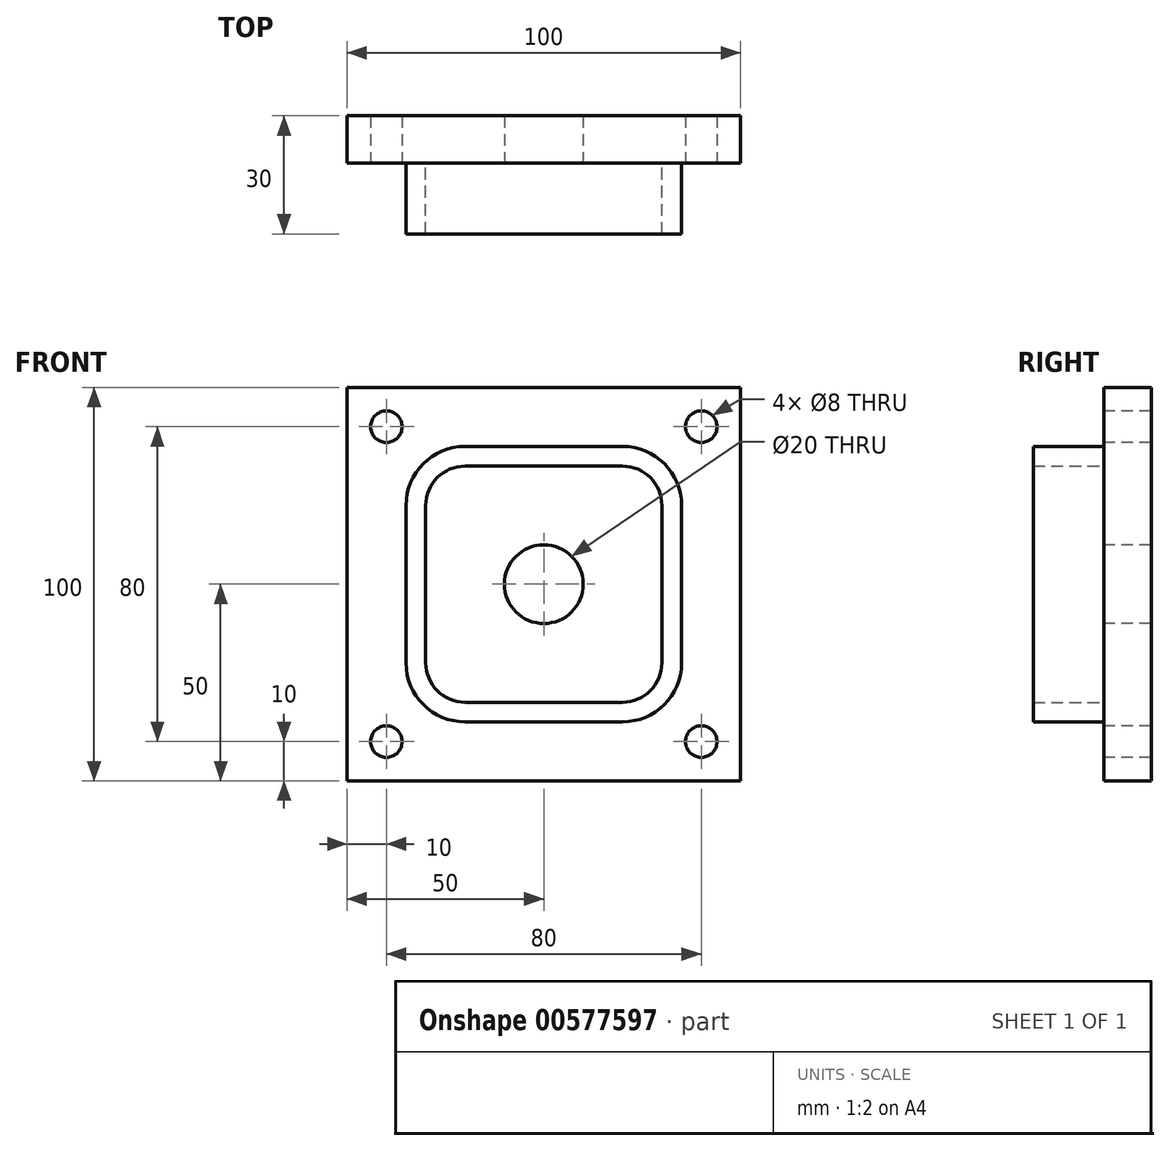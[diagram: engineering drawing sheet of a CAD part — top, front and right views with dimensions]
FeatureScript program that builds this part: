
annotation { "Feature Type Name" : "Feature", "Feature Type Description" : "" }
export const myFeature = defineFeature(function(context is Context, id is Id, definition is map)
    precondition{}
    {
        {
            var Q0;
            Q0=qCreatedBy(makeId("Front.planeOp"),FACE);
            var sketch = newSketch(context, id + "F0", { "sketchPlane" : qUnion([Q0])});
            skLineSegment(sketch, "E0.bottom", {"start": v(0, 0) * mm, "end": v(-100, 0) * mm});
            skLineSegment(sketch, "E0.top", {"start": v(0, 100) * mm, "end": v(-100, 100) * mm});
            skLineSegment(sketch, "E0.left", {"start": v(0, 0) * mm, "end": v(0, 100) * mm});
            skLineSegment(sketch, "E0.right", {"start": v(-100, 0) * mm, "end": v(-100, 100) * mm});
            skSolve(sketch);
        }
        {
            var Q0;
            Q0=makeQuery(id+"F0.imprint","IMPRINT",FACE,{"disambiguationData":[TD([[makeQuery(id+"F0.imprint","IMPRINT",EDGE,{"derivedFrom":sQuery(id+"F0.wireOp",EDGE,"E0.bottom")}),-1.0]])]});
            extrude(context, id + "F1", {"entities" : qUnion([Q0]), "depth" : 12 * mm, "offsetDistance" : 25 * mm});
        }
        {
            var Q0;
            Q0=makeQuery(id+"F1.opExtrude","CAP_FACE",FACE,{"disambiguationData":[OSD([sQuery(id+"F0.wireOp",EDGE,"E0.bottom"),sQuery(id+"F0.wireOp",EDGE,"E0.top"),sQuery(id+"F0.wireOp",EDGE,"E0.left"),sQuery(id+"F0.wireOp",EDGE,"E0.right")])],"isStart":false});
            var sketch = newSketch(context, id + "F2", { "sketchPlane" : qUnion([Q0])});
            skLineSegment(sketch, "E1.bottom", {"start": v(-90, 90) * mm, "end": v(-10, 90) * mm, "construction": true});
            skLineSegment(sketch, "E1.top", {"start": v(-90, 10) * mm, "end": v(-10, 10) * mm, "construction": true});
            skLineSegment(sketch, "E1.left", {"start": v(-90, 90) * mm, "end": v(-90, 10) * mm, "construction": true});
            skLineSegment(sketch, "E1.right", {"start": v(-10, 90) * mm, "end": v(-10, 10) * mm, "construction": true});
            skCircle(sketch, "E2", {"center": v(-90, 90) * mm, "radius": 4 * mm});
            skCircle(sketch, "E3", {"center": v(-90, 10) * mm, "radius": 4 * mm});
            skCircle(sketch, "E4", {"center": v(-10, 90) * mm, "radius": 4 * mm});
            skCircle(sketch, "E5", {"center": v(-10, 10) * mm, "radius": 4 * mm});
            skSolve(sketch);
        }
        {
            var Q0;
            Q0=makeQuery(id+"F2.imprint","IMPRINT",FACE,{"disambiguationData":[TD([[makeQuery(id+"F2.imprint","IMPRINT",EDGE,{"derivedFrom":sQuery(id+"F2.wireOp",EDGE,"E2")}),1.0]])]});
            var Q1;
            Q1=makeQuery(id+"F2.imprint","IMPRINT",FACE,{"disambiguationData":[TD([[makeQuery(id+"F2.imprint","IMPRINT",EDGE,{"derivedFrom":sQuery(id+"F2.wireOp",EDGE,"E4")}),1.0]])]});
            var Q2;
            Q2=makeQuery(id+"F2.imprint","IMPRINT",FACE,{"disambiguationData":[TD([[makeQuery(id+"F2.imprint","IMPRINT",EDGE,{"derivedFrom":sQuery(id+"F2.wireOp",EDGE,"E3")}),1.0]])]});
            var Q3;
            Q3=makeQuery(id+"F2.imprint","IMPRINT",FACE,{"disambiguationData":[TD([[makeQuery(id+"F2.imprint","IMPRINT",EDGE,{"derivedFrom":sQuery(id+"F2.wireOp",EDGE,"E5")}),1.0]])]});
            extrude(context, id + "F3", {"entities" : qUnion([Q0, Q1, Q2, Q3]), "operationType" : NewBodyOperationType.REMOVE, "oppositeDirection" : true, "depth" : 25 * mm, "offsetDistance" : 25 * mm});
        }
        {
            var Q0;
            Q0=makeQuery(id+"F1.opExtrude","CAP_FACE",FACE,{"disambiguationData":[OSD([sQuery(id+"F0.wireOp",EDGE,"E0.bottom"),sQuery(id+"F0.wireOp",EDGE,"E0.top"),sQuery(id+"F0.wireOp",EDGE,"E0.left"),sQuery(id+"F0.wireOp",EDGE,"E0.right")])],"isStart":false});
            var sketch = newSketch(context, id + "F4", { "sketchPlane" : qUnion([Q0])});
            skCircle(sketch, "E6", {"center": v(-50, 50) * mm, "radius": 10 * mm});
            skSolve(sketch);
        }
        {
            var Q0;
            Q0=makeQuery(id+"F4.imprint","IMPRINT",FACE,{"disambiguationData":[TD([[makeQuery(id+"F4.imprint","IMPRINT",EDGE,{"derivedFrom":sQuery(id+"F4.wireOp",EDGE,"E6")}),1.0]])]});
            extrude(context, id + "F5", {"entities" : qUnion([Q0]), "operationType" : NewBodyOperationType.REMOVE, "oppositeDirection" : true, "depth" : 25 * mm, "offsetDistance" : 25 * mm});
        }
        {
            var Q0;
            Q0=makeQuery(id+"F1.opExtrude","CAP_FACE",FACE,{"disambiguationData":[OSD([sQuery(id+"F0.wireOp",EDGE,"E0.bottom"),sQuery(id+"F0.wireOp",EDGE,"E0.top"),sQuery(id+"F0.wireOp",EDGE,"E0.left"),sQuery(id+"F0.wireOp",EDGE,"E0.right")])],"isStart":false});
            var sketch = newSketch(context, id + "F6", { "sketchPlane" : qUnion([Q0])});
            skLineSegment(sketch, "E7", {"start": v(-85, 70) * mm, "end": v(-85, 30) * mm});
            skLineSegment(sketch, "E8", {"start": v(-70, 15) * mm, "end": v(-30, 15) * mm});
            skLineSegment(sketch, "E9", {"start": v(-15, 70) * mm, "end": v(-15, 30) * mm});
            skArc(sketch, "E10", {"start": v(-85, 30) * mm, "mid": v(-80.6, 19.4) * mm, "end": v(-70, 15) * mm});
            skLineSegment(sketch, "E11", {"start": v(-70, 85) * mm, "end": v(-30, 85) * mm});
            skArc(sketch, "E12", {"start": v(-70, 85) * mm, "mid": v(-80.6, 80.6) * mm, "end": v(-85, 70) * mm});
            skArc(sketch, "E13", {"start": v(-15, 70) * mm, "mid": v(-19.4, 80.6) * mm, "end": v(-30, 85) * mm});
            skArc(sketch, "E14", {"start": v(-30, 15) * mm, "mid": v(-19.4, 19.4) * mm, "end": v(-15, 30) * mm});
            skSolve(sketch);
        }
        {
            var Q0;
            Q0=makeQuery(id+"F6.imprint","IMPRINT",FACE,{"disambiguationData":[TD([[makeQuery(id+"F6.imprint","IMPRINT",EDGE,{"derivedFrom":sQuery(id+"F6.wireOp",EDGE,"E7")}),-1.0]])]});
            var sketch = newSketch(context, id + "F7", { "sketchPlane" : qUnion([Q0])});
            skLineSegment(sketch, "E15", {"start": v(-70, 80) * mm, "end": v(-30, 80) * mm});
            skLineSegment(sketch, "E16", {"start": v(-70, 20) * mm, "end": v(-30, 20) * mm});
            skLineSegment(sketch, "E17", {"start": v(-80, 70) * mm, "end": v(-80, 30) * mm});
            skLineSegment(sketch, "E18", {"start": v(-20, 70) * mm, "end": v(-20, 30) * mm});
            skArc(sketch, "E19", {"start": v(-80, 30) * mm, "mid": v(-77.07, 22.93) * mm, "end": v(-70, 20) * mm});
            skArc(sketch, "E20", {"start": v(-70, 80) * mm, "mid": v(-77.07, 77.07) * mm, "end": v(-80, 70) * mm});
            skArc(sketch, "E21", {"start": v(-20, 70) * mm, "mid": v(-22.93, 77.07) * mm, "end": v(-30, 80) * mm});
            skArc(sketch, "E22", {"start": v(-30, 20) * mm, "mid": v(-22.93, 22.93) * mm, "end": v(-20, 30) * mm});
            skSolve(sketch);
        }
        {
            var Q0;
            Q0=makeQuery(id+"F6.imprint","IMPRINT",FACE,{"disambiguationData":[TD([[makeQuery(id+"F6.imprint","IMPRINT",EDGE,{"derivedFrom":sQuery(id+"F6.wireOp",EDGE,"E7")}),1.0]])]});
            extrude(context, id + "F8", {"entities" : qUnion([Q0]), "operationType" : NewBodyOperationType.ADD, "depth" : 18 * mm, "offsetDistance" : 25 * mm});
        }
        {
            var Q0;
            Q0=makeQuery(id+"F7.imprint","IMPRINT",FACE,{"disambiguationData":[TD([[makeQuery(id+"F7.imprint","IMPRINT",EDGE,{"derivedFrom":sQuery(id+"F7.wireOp",EDGE,"E15")}),-1.0]])]});
            extrude(context, id + "F9", {"entities" : qUnion([Q0]), "operationType" : NewBodyOperationType.REMOVE, "depth" : 25 * mm, "offsetDistance" : 25 * mm});
        }
    });
